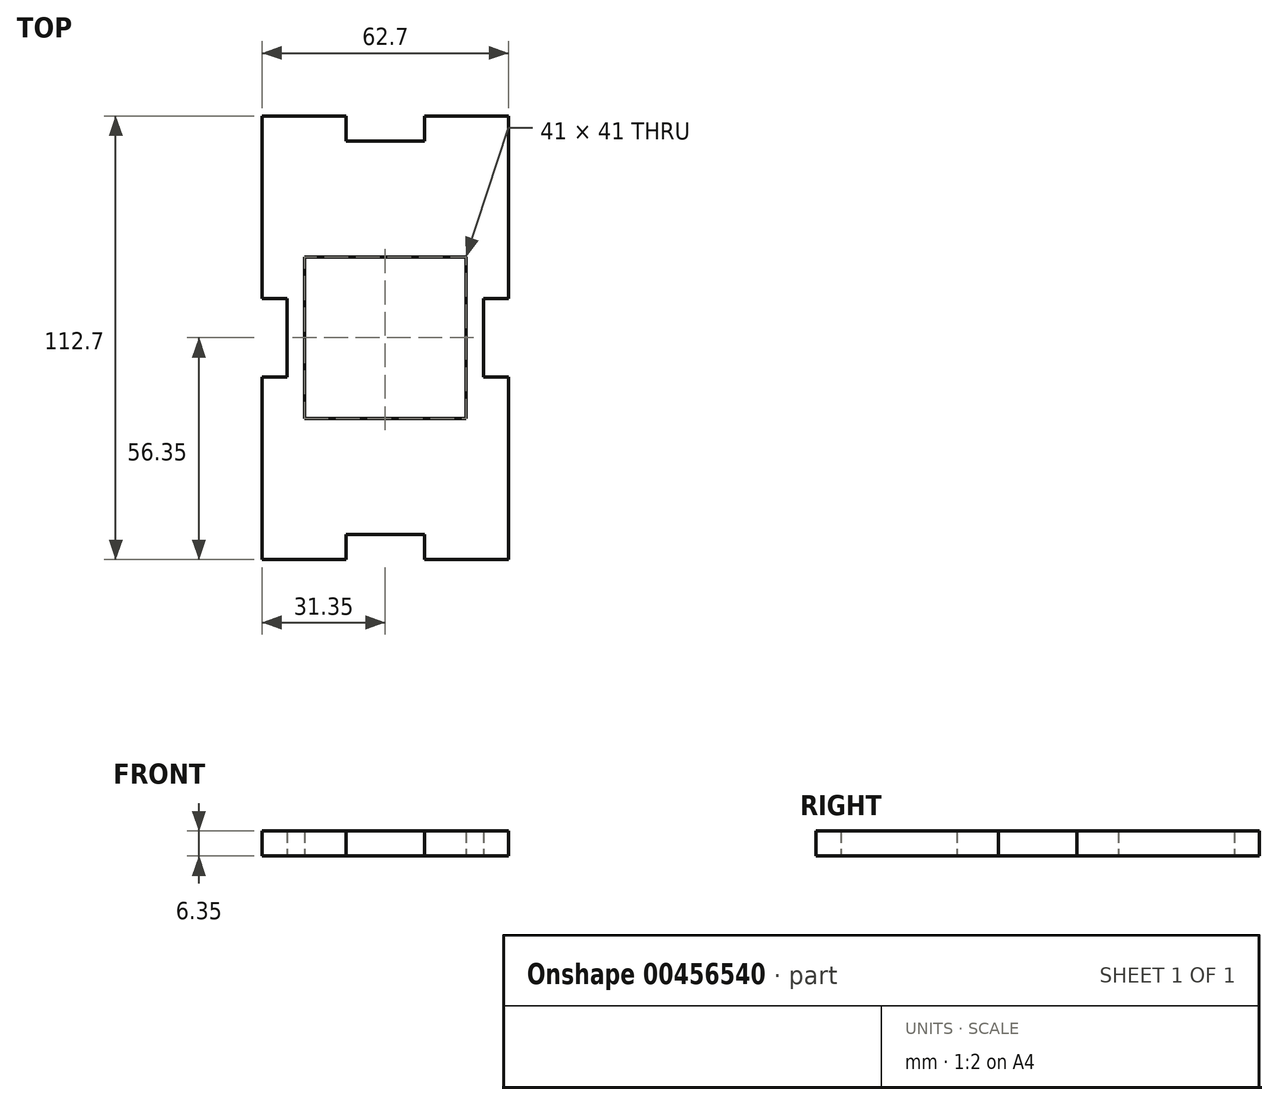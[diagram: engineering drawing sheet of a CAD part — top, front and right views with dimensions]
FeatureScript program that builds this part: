
annotation { "Feature Type Name" : "Feature", "Feature Type Description" : "" }
export const myFeature = defineFeature(function(context is Context, id is Id, definition is map)
    precondition{}
    {
        {
            var Q0;
            Q0=qCreatedBy(makeId("Top.planeOp"),FACE);
            var sketch = newSketch(context, id + "F0", { "sketchPlane" : qUnion([Q0])});
            skLineSegment(sketch, "E0.bottom", {"start": v(-28.65, 53.65) * mm, "end": v(21.35, 53.65) * mm});
            skLineSegment(sketch, "E0.top", {"start": v(-28.65, -46.35) * mm, "end": v(21.35, -46.35) * mm});
            skLineSegment(sketch, "E0.left", {"start": v(-28.65, 53.65) * mm, "end": v(-28.65, -46.35) * mm});
            skLineSegment(sketch, "E0.right", {"start": v(21.35, 53.65) * mm, "end": v(21.35, -46.35) * mm});
            skPoint(sketch, "E0.middle", {"position": v(-3.65, 3.65) * mm});
            skLineSegment(sketch, "E1.bottom", {"start": v(-28.65, 53.65) * mm, "end": v(-35, 53.65) * mm});
            skLineSegment(sketch, "E1.top", {"start": v(-28.65, 13.65) * mm, "end": v(-35, 13.65) * mm});
            skLineSegment(sketch, "E1.left", {"start": v(-28.65, 53.65) * mm, "end": v(-28.65, 13.65) * mm});
            skLineSegment(sketch, "E1.right", {"start": v(-35, 53.65) * mm, "end": v(-35, 13.65) * mm});
            skLineSegment(sketch, "E2.bottom", {"start": v(-28.65, -46.35) * mm, "end": v(-35, -46.35) * mm});
            skLineSegment(sketch, "E2.top", {"start": v(-28.65, -6.35) * mm, "end": v(-35, -6.35) * mm});
            skLineSegment(sketch, "E2.left", {"start": v(-28.65, -46.35) * mm, "end": v(-28.65, -6.35) * mm});
            skLineSegment(sketch, "E2.right", {"start": v(-35, -46.35) * mm, "end": v(-35, -6.35) * mm});
            skLineSegment(sketch, "E3.bottom", {"start": v(-28.65, 53.65) * mm, "end": v(-13.65, 53.65) * mm});
            skLineSegment(sketch, "E3.top", {"start": v(-28.65, 60) * mm, "end": v(-13.65, 60) * mm});
            skLineSegment(sketch, "E3.left", {"start": v(-28.65, 53.65) * mm, "end": v(-28.65, 60) * mm});
            skLineSegment(sketch, "E3.right", {"start": v(-13.65, 53.65) * mm, "end": v(-13.65, 60) * mm});
            skLineSegment(sketch, "E4.bottom", {"start": v(21.35, 53.65) * mm, "end": v(6.35, 53.65) * mm});
            skLineSegment(sketch, "E4.top", {"start": v(21.35, 60) * mm, "end": v(6.35, 60) * mm});
            skLineSegment(sketch, "E4.left", {"start": v(21.35, 53.65) * mm, "end": v(21.35, 60) * mm});
            skLineSegment(sketch, "E4.right", {"start": v(6.35, 53.65) * mm, "end": v(6.35, 60) * mm});
            skLineSegment(sketch, "E5.bottom", {"start": v(-28.65, -46.35) * mm, "end": v(-13.65, -46.35) * mm});
            skLineSegment(sketch, "E5.top", {"start": v(-28.65, -52.7) * mm, "end": v(-13.65, -52.7) * mm});
            skLineSegment(sketch, "E5.left", {"start": v(-28.65, -46.35) * mm, "end": v(-28.65, -52.7) * mm});
            skLineSegment(sketch, "E5.right", {"start": v(-13.65, -46.35) * mm, "end": v(-13.65, -52.7) * mm});
            skLineSegment(sketch, "E6.bottom", {"start": v(21.35, -46.35) * mm, "end": v(6.35, -46.35) * mm});
            skLineSegment(sketch, "E6.top", {"start": v(21.35, -52.7) * mm, "end": v(6.35, -52.7) * mm});
            skLineSegment(sketch, "E6.left", {"start": v(21.35, -46.35) * mm, "end": v(21.35, -52.7) * mm});
            skLineSegment(sketch, "E6.right", {"start": v(6.35, -46.35) * mm, "end": v(6.35, -52.7) * mm});
            skLineSegment(sketch, "E7.bottom", {"start": v(21.35, 53.65) * mm, "end": v(27.7, 53.65) * mm});
            skLineSegment(sketch, "E7.top", {"start": v(21.35, 13.65) * mm, "end": v(27.7, 13.65) * mm});
            skLineSegment(sketch, "E7.left", {"start": v(21.35, 53.65) * mm, "end": v(21.35, 13.65) * mm});
            skLineSegment(sketch, "E7.right", {"start": v(27.7, 53.65) * mm, "end": v(27.7, 13.65) * mm});
            skLineSegment(sketch, "E8.bottom", {"start": v(21.35, -46.35) * mm, "end": v(27.7, -46.35) * mm});
            skLineSegment(sketch, "E8.top", {"start": v(21.35, -6.35) * mm, "end": v(27.7, -6.35) * mm});
            skLineSegment(sketch, "E8.left", {"start": v(21.35, -46.35) * mm, "end": v(21.35, -6.35) * mm});
            skLineSegment(sketch, "E8.right", {"start": v(27.7, -46.35) * mm, "end": v(27.7, -6.35) * mm});
            skLineSegment(sketch, "E9.bottom", {"start": v(21.35, 60) * mm, "end": v(27.7, 60) * mm});
            skLineSegment(sketch, "E9.left", {"start": v(21.35, 60) * mm, "end": v(21.35, 53.65) * mm});
            skLineSegment(sketch, "E9.right", {"start": v(27.7, 60) * mm, "end": v(27.7, 53.65) * mm});
            skLineSegment(sketch, "E10.bottom", {"start": v(-28.65, 60) * mm, "end": v(-35, 60) * mm});
            skLineSegment(sketch, "E10.left", {"start": v(-28.65, 60) * mm, "end": v(-28.65, 53.65) * mm});
            skLineSegment(sketch, "E10.right", {"start": v(-35, 60) * mm, "end": v(-35, 53.65) * mm});
            skLineSegment(sketch, "E11.bottom", {"start": v(-35, -46.35) * mm, "end": v(-28.65, -46.35) * mm});
            skLineSegment(sketch, "E11.top", {"start": v(-35, -52.7) * mm, "end": v(-28.65, -52.7) * mm});
            skLineSegment(sketch, "E11.left", {"start": v(-35, -46.35) * mm, "end": v(-35, -52.7) * mm});
            skLineSegment(sketch, "E12.bottom", {"start": v(27.7, -46.35) * mm, "end": v(21.35, -46.35) * mm});
            skLineSegment(sketch, "E12.top", {"start": v(27.7, -52.7) * mm, "end": v(21.35, -52.7) * mm});
            skLineSegment(sketch, "E12.left", {"start": v(27.7, -46.35) * mm, "end": v(27.7, -52.7) * mm});
            skLineSegment(sketch, "E13.bottom", {"start": v(16.85, 24.15) * mm, "end": v(-24.15, 24.15) * mm});
            skLineSegment(sketch, "E13.top", {"start": v(16.85, -16.85) * mm, "end": v(-24.15, -16.85) * mm});
            skLineSegment(sketch, "E13.left", {"start": v(16.85, 24.15) * mm, "end": v(16.85, -16.85) * mm});
            skLineSegment(sketch, "E13.right", {"start": v(-24.15, 24.15) * mm, "end": v(-24.15, -16.85) * mm});
            skSolve(sketch);
        }
        {
            var Q0;
            Q0 = qSketchRegion(id + "F0", true);
            extrude(context, id + "F1", {"entities" : qUnion([Q0]), "depth" : 6.35 * mm});
        }
    });
